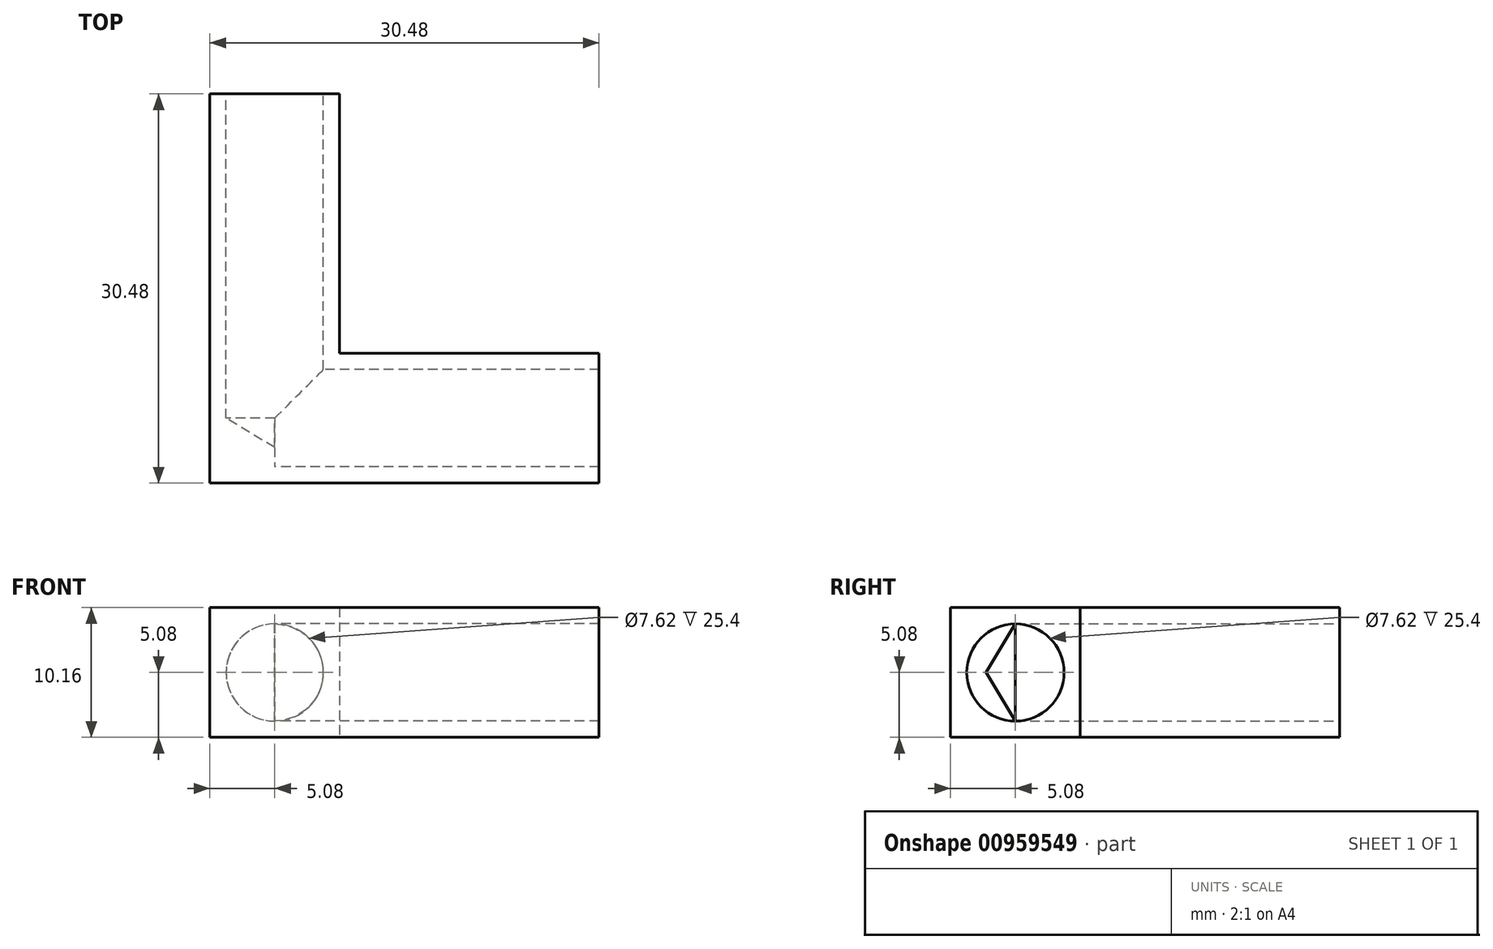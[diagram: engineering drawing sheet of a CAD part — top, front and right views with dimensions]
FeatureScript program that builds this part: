
annotation { "Feature Type Name" : "Feature", "Feature Type Description" : "" }
export const myFeature = defineFeature(function(context is Context, id is Id, definition is map)
    precondition{}
    {
        {
            var Q0;
            Q0=qCreatedBy(makeId("Right.planeOp"),FACE);
            var sketch = newSketch(context, id + "F0", { "sketchPlane" : qUnion([Q0])});
            skLineSegment(sketch, "E0.bottom", {"start": v(5.08, 5.08) * mm, "end": v(-5.08, 5.08) * mm});
            skLineSegment(sketch, "E0.top", {"start": v(5.08, -5.08) * mm, "end": v(-5.08, -5.08) * mm});
            skLineSegment(sketch, "E0.left", {"start": v(5.08, 5.08) * mm, "end": v(5.08, -5.08) * mm});
            skLineSegment(sketch, "E0.right", {"start": v(-5.08, 5.08) * mm, "end": v(-5.08, -5.08) * mm});
            skPoint(sketch, "E0.middle", {"position": v(0, 0) * mm});
            skSolve(sketch);
        }
        {
            var Q0;
            Q0=makeQuery(id+"F0.imprint","IMPRINT",FACE,{"disambiguationData":[TD([[makeQuery(id+"F0.imprint","IMPRINT",EDGE,{"derivedFrom":sQuery(id+"F0.wireOp",EDGE,"E0.bottom")}),1.0]])]});
            extrude(context, id + "F1", {"entities" : qUnion([Q0]), "depth" : 25.4 * mm, "offsetDistance" : 25.4 * mm, "hasSecondDirection" : true, "secondDirectionOppositeDirection" : true, "secondDirectionDepth" : 5.08 * mm});
        }
        {
            var Q0;
            Q0=qCreatedBy(makeId("Right.planeOp"),FACE);
            var sketch = newSketch(context, id + "F2", { "sketchPlane" : qUnion([Q0])});
            skPoint(sketch, "E1", {"position": v(0, 0) * mm});
            skSolve(sketch);
        }
        {
            var Q0;
            Q0=sQuery(id+"F2.wireOp",VERTEX,"E1");
            var Q1;
            Q1=makeQuery(id+"F1.opExtrude","SWEPT_BODY",BODY,{"disambiguationData":[OSD([sQuery(id+"F0.wireOp",EDGE,"E0.bottom"),sQuery(id+"F0.wireOp",EDGE,"E0.top"),sQuery(id+"F0.wireOp",EDGE,"E0.left"),sQuery(id+"F0.wireOp",EDGE,"E0.right")])]});
            hole(context, id + "F3", {"style" : HoleStyle.SIMPLE, "endStyle" : HoleEndStyle.THROUGH, "oppositeDirection" : true, "holeDiameter" : 7.62 * mm, "majorDiameter" : 6.35 * mm, "isTappedThrough" : true, "tappedDepth" : 12.7 * mm, "tapClearance" : 3, "locations" : qUnion([Q0]), "scope" : qUnion([Q1])});
        }
        {
            var Q0;
            Q0=qCreatedBy(makeId("Front.planeOp"),FACE);
            var sketch = newSketch(context, id + "F4", { "sketchPlane" : qUnion([Q0])});
            skLineSegment(sketch, "E2.bottom", {"start": v(-5.08, 5.08) * mm, "end": v(5.08, 5.08) * mm});
            skLineSegment(sketch, "E2.top", {"start": v(-5.08, -5.08) * mm, "end": v(5.08, -5.08) * mm});
            skLineSegment(sketch, "E2.left", {"start": v(-5.08, 5.08) * mm, "end": v(-5.08, -5.08) * mm});
            skLineSegment(sketch, "E2.right", {"start": v(5.08, 5.08) * mm, "end": v(5.08, -5.08) * mm});
            skPoint(sketch, "E2.middle", {"position": v(0, 0) * mm});
            skSolve(sketch);
        }
        {
            var Q0;
            Q0 = qSketchRegion(id + "F4", true);
            extrude(context, id + "F5", {"entities" : qUnion([Q0]), "operationType" : NewBodyOperationType.ADD, "oppositeDirection" : true, "depth" : 25.4 * mm, "offsetDistance" : 25.4 * mm, "hasSecondDirection" : true, "secondDirectionOppositeDirection" : true, "secondDirectionDepth" : 5.08 * mm});
        }
        {
            var Q0;
            Q0=makeQuery(id+"F5.opExtrude","CAP_FACE",FACE,{"disambiguationData":[OSD([sQuery(id+"F4.wireOp",EDGE,"E2.bottom"),sQuery(id+"F4.wireOp",EDGE,"E2.top"),sQuery(id+"F4.wireOp",EDGE,"E2.left"),sQuery(id+"F4.wireOp",EDGE,"E2.right")])],"isStart":false});
            var sketch = newSketch(context, id + "F6", { "sketchPlane" : qUnion([Q0])});
            skPoint(sketch, "E3", {"position": v(0, 0) * mm});
            skSolve(sketch);
        }
        {
            var Q0;
            Q0=sQuery(id+"F6.wireOp",VERTEX,"E3");
            var Q1;
            Q1=makeQuery(id+"F1.opExtrude","SWEPT_BODY",BODY,{"disambiguationData":[OSD([sQuery(id+"F0.wireOp",EDGE,"E0.bottom"),sQuery(id+"F0.wireOp",EDGE,"E0.top"),sQuery(id+"F0.wireOp",EDGE,"E0.left"),sQuery(id+"F0.wireOp",EDGE,"E0.right")])]});
            hole(context, id + "F7", {"style" : HoleStyle.SIMPLE, "endStyle" : HoleEndStyle.BLIND, "holeDiameter" : 7.62 * mm, "majorDiameter" : 6.35 * mm, "holeDepth" : 25.4 * mm, "isTappedThrough" : true, "tappedDepth" : 12.7 * mm, "tapClearance" : 3, "locations" : qUnion([Q0]), "scope" : qUnion([Q1])});
        }
    });
